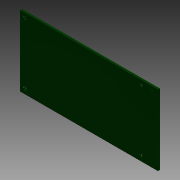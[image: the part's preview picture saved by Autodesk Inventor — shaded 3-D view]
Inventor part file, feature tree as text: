
AUTODESK INVENTOR PART (.ipt)
format: ipt  version: 2015 (Build 190159000, 159)  size: 134,144 bytes
history: native  units: in
note: dims shown in document units (in); Inventor stores cm internally (conversion verified against a paired STEP export)
features: extrude x2, sketch x2
ambient origin geometry x8: Origin, YZ Plane, XZ Plane, XY Plane, X Axis, Y Axis, Z Axis, Center Point
bodies: Solid1 (feature_tree)
feature tree (4):
  extrude  "Extrusion1"  Depth=4.4in
  extrude  "Extrusion3"  Depth=2.25in
  sketch  "Sketch1"  dims[d0=0.0646in d1=0.0in d2=4.4in]
  sketch  "Sketch3"  dims[d4=2.25in d5=1.95in d6=0.1102in d8=0.1102in d10=1.95in d15=0.0787in d16=0.1969in d17=0.1969in d18=0.0394in d19=0.1181in d20=0.0in d21=0.15in d22=0.15in d23=0.15in d28=0.15in d30=2.5in d33=1.3469in d34=1.3469in d35=0.078in d36=0.2in d37=0.1067in d38=0.1102in d39=0.15in d40=0.55in d41=2.5in d42=0.063in d43=0.2in d44=0.1067in]
